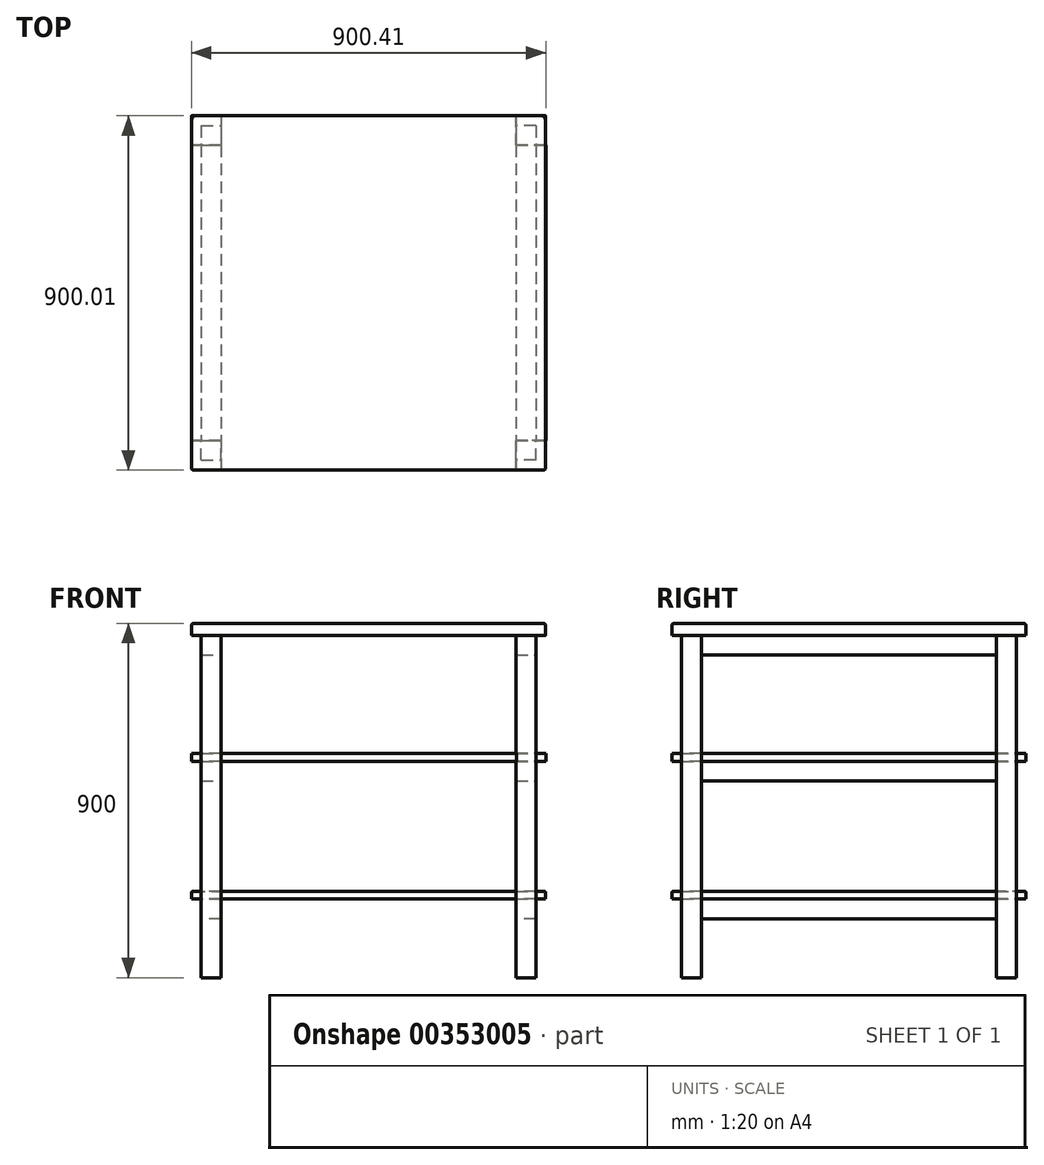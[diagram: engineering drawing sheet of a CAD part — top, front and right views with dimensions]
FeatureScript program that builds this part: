
annotation { "Feature Type Name" : "Feature", "Feature Type Description" : "" }
export const myFeature = defineFeature(function(context is Context, id is Id, definition is map)
    precondition{}
    {
        {
            var Q0;
            Q0=qCreatedBy(makeId("Top.planeOp"),FACE);
            var sketch = newSketch(context, id + "F0", { "sketchPlane" : qUnion([Q0])});
            skLineSegment(sketch, "E0.bottom", {"start": v(-72.92, 43.57) * mm, "end": v(-22.92, 43.57) * mm});
            skLineSegment(sketch, "E0.top", {"start": v(-72.92, -6.43) * mm, "end": v(-22.92, -6.43) * mm});
            skLineSegment(sketch, "E0.left", {"start": v(-72.92, 43.57) * mm, "end": v(-72.92, -6.43) * mm});
            skLineSegment(sketch, "E0.right", {"start": v(-22.92, 43.57) * mm, "end": v(-22.92, -6.43) * mm});
            skLineSegment(sketch, "E1.MirrorCS", {"start": v(777.08, 43.57) * mm, "end": v(727.08, 43.57) * mm});
            skLineSegment(sketch, "E2.MirrorCS", {"start": v(777.08, -6.43) * mm, "end": v(727.08, -6.43) * mm});
            skLineSegment(sketch, "E3.MirrorCS", {"start": v(777.08, 43.57) * mm, "end": v(777.08, -6.43) * mm});
            skLineSegment(sketch, "E4.MirrorCS", {"start": v(727.08, 43.57) * mm, "end": v(727.08, -6.43) * mm});
            skLineSegment(sketch, "E5.MirrorCS", {"start": v(-22.92, -806.43) * mm, "end": v(-22.92, -756.43) * mm});
            skLineSegment(sketch, "E6.MirrorCS", {"start": v(-72.92, -806.43) * mm, "end": v(-72.92, -756.43) * mm});
            skLineSegment(sketch, "E7.MirrorCS", {"start": v(-72.92, -806.43) * mm, "end": v(-22.92, -806.43) * mm});
            skLineSegment(sketch, "E8.MirrorCS", {"start": v(-72.92, -756.43) * mm, "end": v(-22.92, -756.43) * mm});
            skLineSegment(sketch, "E9.MirrorCS", {"start": v(727.08, -806.43) * mm, "end": v(727.08, -756.43) * mm});
            skLineSegment(sketch, "E10.MirrorCS", {"start": v(777.08, -806.43) * mm, "end": v(777.08, -756.43) * mm});
            skLineSegment(sketch, "E11.MirrorCS", {"start": v(777.08, -806.43) * mm, "end": v(727.08, -806.43) * mm});
            skLineSegment(sketch, "E12.MirrorCS", {"start": v(777.08, -756.43) * mm, "end": v(727.08, -756.43) * mm});
            skSolve(sketch);
        }
        {
            var Q0;
            Q0=makeQuery(id+"F0.imprint","IMPRINT",FACE,{"disambiguationData":[TD([[makeQuery(id+"F0.imprint","IMPRINT",EDGE,{"derivedFrom":sQuery(id+"F0.wireOp",EDGE,"E5.MirrorCS")}),1.0]])]});
            var Q1;
            Q1=makeQuery(id+"F0.imprint","IMPRINT",FACE,{"disambiguationData":[TD([[makeQuery(id+"F0.imprint","IMPRINT",EDGE,{"derivedFrom":sQuery(id+"F0.wireOp",EDGE,"E0.bottom")}),-1.0]])]});
            var Q2;
            Q2=makeQuery(id+"F0.imprint","IMPRINT",FACE,{"disambiguationData":[TD([[makeQuery(id+"F0.imprint","IMPRINT",EDGE,{"derivedFrom":sQuery(id+"F0.wireOp",EDGE,"E9.MirrorCS")}),-1.0]])]});
            var Q3;
            Q3=makeQuery(id+"F0.imprint","IMPRINT",FACE,{"disambiguationData":[TD([[makeQuery(id+"F0.imprint","IMPRINT",EDGE,{"derivedFrom":sQuery(id+"F0.wireOp",EDGE,"E1.MirrorCS")}),1.0]])]});
            extrude(context, id + "F1", {"entities" : qUnion([Q0, Q1, Q2, Q3]), "oppositeDirection" : true, "depth" : 870 * mm});
        }
        {
            var Q0;
            Q0=makeQuery(id+"F1.opExtrude","SWEPT_FACE",FACE,{"disambiguationData":[OSD([sQuery(id+"F0.wireOp",EDGE,"E9.MirrorCS")])]});
            var sketch = newSketch(context, id + "F2", { "sketchPlane" : qUnion([Q0])});
            skLineSegment(sketch, "E13.bottom", {"start": v(756.43, -670) * mm, "end": v(806.43, -670) * mm});
            skLineSegment(sketch, "E13.top", {"start": v(756.43, -720) * mm, "end": v(806.43, -720) * mm});
            skLineSegment(sketch, "E13.left", {"start": v(756.43, -670) * mm, "end": v(756.43, -720) * mm});
            skLineSegment(sketch, "E13.right", {"start": v(806.43, -670) * mm, "end": v(806.43, -720) * mm});
            skLineSegment(sketch, "E14.bottom", {"start": v(-43.57, -670) * mm, "end": v(6.43, -670) * mm});
            skLineSegment(sketch, "E14.top", {"start": v(-43.57, -720) * mm, "end": v(6.43, -720) * mm});
            skLineSegment(sketch, "E14.left", {"start": v(-43.57, -670) * mm, "end": v(-43.57, -720) * mm});
            skLineSegment(sketch, "E14.right", {"start": v(6.43, -670) * mm, "end": v(6.43, -720) * mm});
            skLineSegment(sketch, "E15.bottom", {"start": v(-43.57, 0) * mm, "end": v(6.43, 0) * mm});
            skLineSegment(sketch, "E15.top", {"start": v(-43.57, -50) * mm, "end": v(6.43, -50) * mm});
            skLineSegment(sketch, "E15.left", {"start": v(-43.57, 0) * mm, "end": v(-43.57, -50) * mm});
            skLineSegment(sketch, "E15.right", {"start": v(6.43, 0) * mm, "end": v(6.43, -50) * mm});
            skLineSegment(sketch, "E16.bottom", {"start": v(756.43, 0) * mm, "end": v(806.43, 0) * mm});
            skLineSegment(sketch, "E16.top", {"start": v(756.43, -50) * mm, "end": v(806.43, -50) * mm});
            skLineSegment(sketch, "E16.left", {"start": v(756.43, 0) * mm, "end": v(756.43, -50) * mm});
            skLineSegment(sketch, "E16.right", {"start": v(806.43, 0) * mm, "end": v(806.43, -50) * mm});
            skSolve(sketch);
        }
        {
            var Q0;
            Q0=makeQuery(id+"F1.opExtrude","SWEPT_FACE",FACE,{"disambiguationData":[OSD([sQuery(id+"F0.wireOp",EDGE,"E8.MirrorCS")])]});
            var sketch = newSketch(context, id + "F3", { "sketchPlane" : qUnion([Q0])});
            skLineSegment(sketch, "E17.bottom", {"start": v(-777.08, -670) * mm, "end": v(-727.08, -670) * mm});
            skLineSegment(sketch, "E17.top", {"start": v(-777.08, -720) * mm, "end": v(-727.08, -720) * mm});
            skLineSegment(sketch, "E17.left", {"start": v(-777.08, -670) * mm, "end": v(-777.08, -720) * mm});
            skLineSegment(sketch, "E17.right", {"start": v(-727.08, -670) * mm, "end": v(-727.08, -720) * mm});
            skLineSegment(sketch, "E18.bottom", {"start": v(22.92, -670) * mm, "end": v(72.92, -670) * mm});
            skLineSegment(sketch, "E18.top", {"start": v(22.92, -720) * mm, "end": v(72.92, -720) * mm});
            skLineSegment(sketch, "E18.left", {"start": v(22.92, -670) * mm, "end": v(22.92, -720) * mm});
            skLineSegment(sketch, "E18.right", {"start": v(72.92, -670) * mm, "end": v(72.92, -720) * mm});
            skLineSegment(sketch, "E19.bottom", {"start": v(72.92, 0) * mm, "end": v(22.92, 0) * mm});
            skLineSegment(sketch, "E19.top", {"start": v(72.92, -50) * mm, "end": v(22.92, -50) * mm});
            skLineSegment(sketch, "E19.left", {"start": v(72.92, 0) * mm, "end": v(72.92, -50) * mm});
            skLineSegment(sketch, "E19.right", {"start": v(22.92, 0) * mm, "end": v(22.92, -50) * mm});
            skLineSegment(sketch, "E20.bottom", {"start": v(-727.08, 0) * mm, "end": v(-777.08, 0) * mm});
            skLineSegment(sketch, "E20.top", {"start": v(-727.08, -50) * mm, "end": v(-777.08, -50) * mm});
            skLineSegment(sketch, "E20.left", {"start": v(-727.08, 0) * mm, "end": v(-727.08, -50) * mm});
            skLineSegment(sketch, "E20.right", {"start": v(-777.08, 0) * mm, "end": v(-777.08, -50) * mm});
            skLineSegment(sketch, "E21.bottom", {"start": v(72.92, -320) * mm, "end": v(22.92, -320) * mm});
            skLineSegment(sketch, "E21.top", {"start": v(72.92, -370) * mm, "end": v(22.92, -370) * mm});
            skLineSegment(sketch, "E21.left", {"start": v(72.92, -320) * mm, "end": v(72.92, -370) * mm});
            skLineSegment(sketch, "E21.right", {"start": v(22.92, -320) * mm, "end": v(22.92, -370) * mm});
            skLineSegment(sketch, "E22.bottom", {"start": v(-727.08, -320) * mm, "end": v(-777.08, -320) * mm});
            skLineSegment(sketch, "E22.top", {"start": v(-727.08, -370) * mm, "end": v(-777.08, -370) * mm});
            skLineSegment(sketch, "E22.left", {"start": v(-727.08, -320) * mm, "end": v(-727.08, -370) * mm});
            skLineSegment(sketch, "E22.right", {"start": v(-777.08, -320) * mm, "end": v(-777.08, -370) * mm});
            skSolve(sketch);
        }
        {
            var Q0;
            Q0=makeQuery(id+"F0.imprint","IMPRINT",FACE,{"disambiguationData":[TD([[makeQuery(id+"F0.imprint","IMPRINT",EDGE,{"derivedFrom":sQuery(id+"F0.wireOp",EDGE,"E1.MirrorCS")}),1.0]])]});
            var sketch = newSketch(context, id + "F4", { "sketchPlane" : qUnion([Q0])});
            skLineSegment(sketch, "E23.bottom", {"start": v(-97.92, 68.57) * mm, "end": v(802.08, 68.57) * mm});
            skLineSegment(sketch, "E23.top", {"start": v(-97.92, -831.43) * mm, "end": v(802.08, -831.43) * mm});
            skLineSegment(sketch, "E23.left", {"start": v(-97.92, 68.57) * mm, "end": v(-97.92, -831.43) * mm});
            skLineSegment(sketch, "E23.right", {"start": v(802.08, 68.57) * mm, "end": v(802.08, -831.43) * mm});
            skSolve(sketch);
        }
        {
            var Q0;
            Q0 = qSketchRegion(id + "F4", true);
            extrude(context, id + "F5", {"entities" : qUnion([Q0]), "depth" : 30 * mm});
        }
        {
            var Q0;
            Q0=sQuery(id+"F2.wireOp",EDGE,"E13.top");
            var Q1;
            Q1=sQuery(id+"F2.wireOp",EDGE,"E15.top");
            var Q2;
            Q2=sQuery(id+"F2.wireOp",EDGE,"E16.bottom");
            var Q3;
            Q3=sQuery(id+"F2.wireOp",EDGE,"E14.bottom");
            var Q4;
            Q4=sQuery(id+"F2.wireOp",EDGE,"E16.right");
            var Q5;
            Q5=sQuery(id+"F2.wireOp",EDGE,"E14.right");
            var Q6;
            Q6=sQuery(id+"F2.wireOp",EDGE,"E14.left");
            var Q7;
            Q7=sQuery(id+"F2.wireOp",EDGE,"E15.right");
            var Q8;
            Q8=sQuery(id+"F2.wireOp",EDGE,"E14.top");
            var Q9;
            Q9=sQuery(id+"F2.wireOp",EDGE,"E15.left");
            var Q10;
            Q10=sQuery(id+"F2.wireOp",EDGE,"E13.left");
            var Q11;
            Q11=sQuery(id+"F2.wireOp",EDGE,"E16.left");
            var Q12;
            Q12=sQuery(id+"F2.wireOp",EDGE,"E16.top");
            var Q13;
            Q13=sQuery(id+"F2.wireOp",EDGE,"E13.bottom");
            var Q14;
            Q14=sQuery(id+"F2.wireOp",EDGE,"E13.right");
            var Q15;
            Q15=sQuery(id+"F2.wireOp",EDGE,"E15.bottom");
            extrude(context, id + "F6", {"bodyType" : ToolBodyType.SURFACE, "surfaceEntities" : qUnion([Q0, Q1, Q2, Q3, Q4, Q5, Q6, Q7, Q8, Q9, Q10, Q11, Q12, Q13, Q14, Q15]), "depth" : 750 * mm});
        }
        {
            var Q0;
            Q0=makeQuery(id+"F6.opExtrude","SWEPT_FACE",FACE,{"disambiguationData":[OSD([sQuery(id+"F2.wireOp",EDGE,"E13.bottom")])]});
            var sketch = newSketch(context, id + "F7", { "sketchPlane" : qUnion([Q0])});
            skLineSegment(sketch, "E24", {"start": v(802.08, -756.43) * mm, "end": v(802.08, -6.43) * mm});
            skLineSegment(sketch, "E25", {"start": v(802.08, -756.43) * mm, "end": v(727.08, -756.43) * mm});
            skLineSegment(sketch, "E26", {"start": v(727.08, -831.43) * mm, "end": v(727.08, -756.43) * mm});
            skLineSegment(sketch, "E27", {"start": v(727.08, -831.43) * mm, "end": v(-22.92, -831.43) * mm});
            skLineSegment(sketch, "E28", {"start": v(-22.92, -756.43) * mm, "end": v(-22.92, -831.43) * mm});
            skLineSegment(sketch, "E29", {"start": v(-22.92, -756.43) * mm, "end": v(-97.92, -756.43) * mm});
            skLineSegment(sketch, "E30", {"start": v(-97.92, -6.43) * mm, "end": v(-97.92, -756.43) * mm});
            skLineSegment(sketch, "E31", {"start": v(-97.92, -6.43) * mm, "end": v(-22.92, -6.43) * mm});
            skLineSegment(sketch, "E32", {"start": v(-22.92, 68.57) * mm, "end": v(-22.92, -6.43) * mm});
            skLineSegment(sketch, "E33", {"start": v(-22.92, 68.57) * mm, "end": v(727.08, 68.57) * mm});
            skLineSegment(sketch, "E34", {"start": v(727.08, -6.43) * mm, "end": v(727.08, 68.57) * mm});
            skLineSegment(sketch, "E35", {"start": v(727.08, -6.43) * mm, "end": v(802.08, -6.43) * mm});
            skSolve(sketch);
        }
        {
            var Q0;
            Q0 = qSketchRegion(id + "F7", true);
            extrude(context, id + "F8", {"entities" : qUnion([Q0]), "depth" : 20 * mm});
        }
        {
            var Q0;
            Q0=makeQuery(id+"F5.opExtrude","CAP_EDGE",EDGE,{"disambiguationData":[OSD([sQuery(id+"F4.wireOp",EDGE,"E23.top")])],"isStart":false});
            fillet(context, id + "F9", {"entities" : qUnion([Q0]), "radius" : 5 * mm, "tangentPropagation" : true, "allowEdgeOverflow" : false});
        }
        {
            var Q0;
            Q0=makeQuery(id+"F5.opExtrude","CAP_EDGE",EDGE,{"disambiguationData":[OSD([sQuery(id+"F4.wireOp",EDGE,"E23.right")])],"isStart":false});
            var Q1;
            Q1=makeQuery(id+"F5.opExtrude","CAP_EDGE",EDGE,{"disambiguationData":[OSD([sQuery(id+"F4.wireOp",EDGE,"E23.left")])],"isStart":false});
            var Q2;
            Q2=makeQuery(id+"F5.opExtrude","CAP_EDGE",EDGE,{"disambiguationData":[OSD([sQuery(id+"F4.wireOp",EDGE,"E23.bottom")])],"isStart":false});
            fillet(context, id + "F10", {"entities" : qUnion([Q0, Q1, Q2]), "radius" : 5 * mm, "tangentPropagation" : true, "allowEdgeOverflow" : false});
        }
        {
            var Q0;
            Q0=makeQuery(id+"F8.opExtrude","CAP_EDGE",EDGE,{"disambiguationData":[OSD([sQuery(id+"F7.wireOp",EDGE,"E24")])],"isStart":false});
            var Q1;
            Q1=makeQuery(id+"F8.opExtrude","CAP_EDGE",EDGE,{"disambiguationData":[OSD([sQuery(id+"F7.wireOp",EDGE,"E33")])],"isStart":false});
            var Q2;
            Q2=makeQuery(id+"F8.opExtrude","CAP_EDGE",EDGE,{"disambiguationData":[OSD([sQuery(id+"F7.wireOp",EDGE,"E27")])],"isStart":false});
            var Q3;
            Q3=makeQuery(id+"F8.opExtrude","CAP_EDGE",EDGE,{"disambiguationData":[OSD([sQuery(id+"F7.wireOp",EDGE,"E30")])],"isStart":false});
            fillet(context, id + "F11", {"entities" : qUnion([Q0, Q1, Q2, Q3]), "radius" : 5 * mm, "tangentPropagation" : true, "allowEdgeOverflow" : false});
        }
        {
            var Q0;
            Q0 = qSketchRegion(id + "F3", true);
            extrude(context, id + "F12", {"entities" : qUnion([Q0]), "depth" : 750 * mm});
        }
        {
            var Q0;
            Q0=makeQuery(id+"F12.opExtrude","SWEPT_FACE",FACE,{"disambiguationData":[OSD([sQuery(id+"F3.wireOp",EDGE,"E21.bottom")])]});
            var sketch = newSketch(context, id + "F13", { "sketchPlane" : qUnion([Q0])});
            skLineSegment(sketch, "E36", {"start": v(802.5, -756.44) * mm, "end": v(802.5, -6.44) * mm});
            skLineSegment(sketch, "E37", {"start": v(802.5, -6.44) * mm, "end": v(727.5, -6.44) * mm});
            skLineSegment(sketch, "E38", {"start": v(727.5, -6.44) * mm, "end": v(727.5, 68.56) * mm});
            skLineSegment(sketch, "E39", {"start": v(727.5, 68.56) * mm, "end": v(-22.5, 68.56) * mm});
            skLineSegment(sketch, "E40", {"start": v(-22.5, 68.56) * mm, "end": v(-22.5, -6.44) * mm});
            skLineSegment(sketch, "E41", {"start": v(-22.5, -6.44) * mm, "end": v(-97.5, -6.44) * mm});
            skLineSegment(sketch, "E42", {"start": v(-97.5, -6.44) * mm, "end": v(-97.5, -756.44) * mm});
            skLineSegment(sketch, "E43", {"start": v(-97.5, -756.44) * mm, "end": v(-22.5, -756.44) * mm});
            skLineSegment(sketch, "E44", {"start": v(-22.5, -756.44) * mm, "end": v(-22.5, -831.44) * mm});
            skLineSegment(sketch, "E45", {"start": v(-22.5, -831.44) * mm, "end": v(727.5, -831.44) * mm});
            skLineSegment(sketch, "E46", {"start": v(727.5, -831.44) * mm, "end": v(727.5, -756.44) * mm});
            skLineSegment(sketch, "E47", {"start": v(727.5, -756.44) * mm, "end": v(802.5, -756.44) * mm});
            skSolve(sketch);
        }
        {
            var Q0;
            Q0 = qSketchRegion(id + "F13", true);
            extrude(context, id + "F14", {"entities" : qUnion([Q0]), "depth" : 20 * mm});
        }
    });
